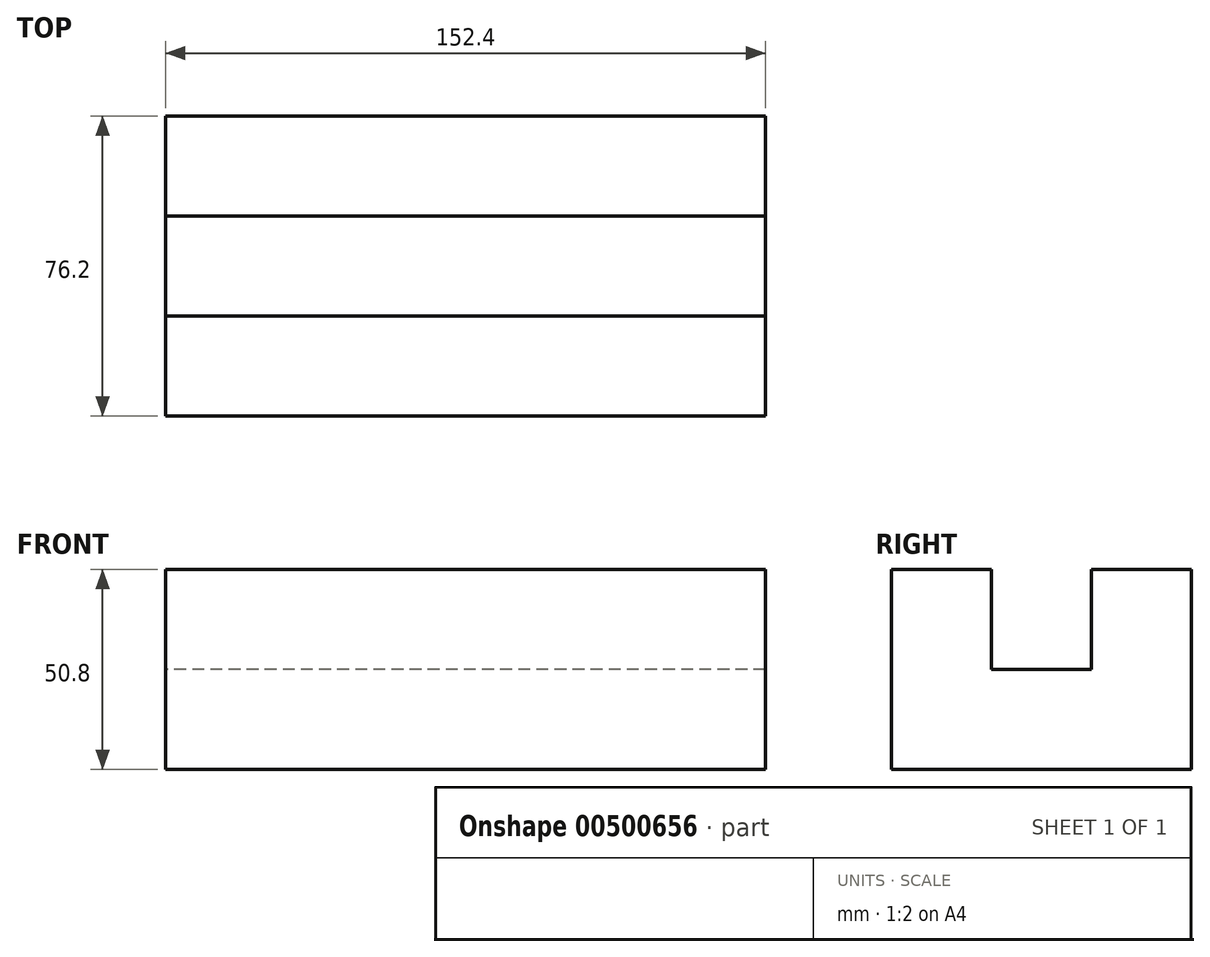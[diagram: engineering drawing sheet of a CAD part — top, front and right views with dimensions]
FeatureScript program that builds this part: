
annotation { "Feature Type Name" : "Feature", "Feature Type Description" : "" }
export const myFeature = defineFeature(function(context is Context, id is Id, definition is map)
    precondition{}
    {
        {
            var Q0;
            Q0=qCreatedBy(makeId("Right.planeOp"),FACE);
            var sketch = newSketch(context, id + "F0", { "sketchPlane" : qUnion([Q0])});
            skLineSegment(sketch, "E0", {"start": v(-50.8, 69.75) * mm, "end": v(-50.8, 18.95) * mm});
            skLineSegment(sketch, "E1", {"start": v(-50.8, 18.95) * mm, "end": v(25.4, 18.95) * mm});
            skLineSegment(sketch, "E2", {"start": v(25.4, 18.95) * mm, "end": v(25.4, 69.75) * mm});
            skLineSegment(sketch, "E3", {"start": v(25.4, 69.75) * mm, "end": v(0, 69.75) * mm});
            skLineSegment(sketch, "E4", {"start": v(0, 69.75) * mm, "end": v(0, 44.35) * mm});
            skLineSegment(sketch, "E5", {"start": v(0, 44.35) * mm, "end": v(-25.4, 44.35) * mm});
            skLineSegment(sketch, "E6", {"start": v(-25.4, 44.35) * mm, "end": v(-25.4, 69.75) * mm});
            skLineSegment(sketch, "E7", {"start": v(-25.4, 69.75) * mm, "end": v(-50.8, 69.75) * mm});
            skSolve(sketch);
        }
        {
            var Q0;
            Q0 = qSketchRegion(id + "F0", true);
            extrude(context, id + "F1", {"entities" : qUnion([Q0]), "depth" : 152.4 * mm});
        }
    });
